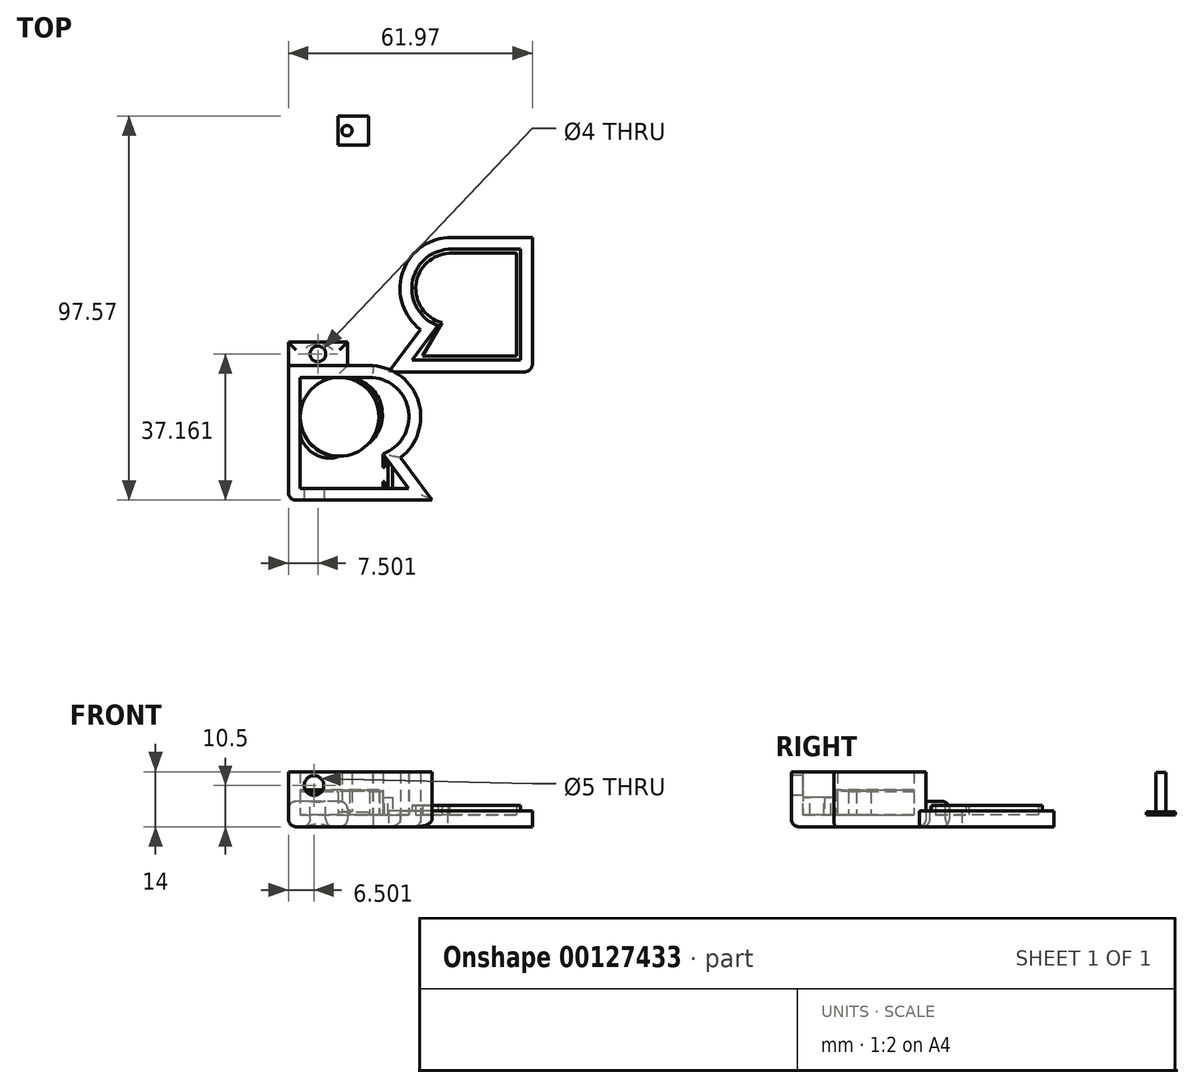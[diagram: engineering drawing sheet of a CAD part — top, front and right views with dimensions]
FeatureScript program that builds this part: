
annotation { "Feature Type Name" : "Feature", "Feature Type Description" : "" }
export const myFeature = defineFeature(function(context is Context, id is Id, definition is map)
    precondition{}
    {
        {
            var Q0;
            Q0=qCreatedBy(makeId("Top.planeOp"),FACE);
            var sketch = newSketch(context, id + "F0", { "sketchPlane" : qUnion([Q0])});
            skArc(sketch, "E0", {"start": v(-49.02, -36.56) * mm, "mid": v(-42.48, -25.81) * mm, "end": v(-51.63, -17.18) * mm});
            skLineSegment(sketch, "E1", {"start": v(-51.63, -17.18) * mm, "end": v(-70.02, -17.18) * mm});
            skLineSegment(sketch, "E2", {"start": v(-70.02, -17.18) * mm, "end": v(-70.02, -45.34) * mm});
            skLineSegment(sketch, "E3", {"start": v(-49.02, -36.56) * mm, "end": v(-42.48, -45.34) * mm});
            skPoint(sketch, "E3.endSnap0", {"position": v(-42.48, -25.81) * mm});
            skLineSegment(sketch, "E4", {"start": v(-70.02, -45.34) * mm, "end": v(-42.48, -45.34) * mm});
            skLineSegment(sketch, "E5", {"start": v(-62.53, -36.96) * mm, "end": v(-62.53, -43.4) * mm});
            skLineSegment(sketch, "E6", {"start": v(-62.53, -43.4) * mm, "end": v(-53.92, -43.4) * mm});
            skLineSegment(sketch, "E7", {"start": v(-53.92, -43.4) * mm, "end": v(-58.71, -36.96) * mm});
            skLineSegment(sketch, "E8", {"start": v(-58.71, -36.96) * mm, "end": v(-62.53, -36.96) * mm});
            skLineSegment(sketch, "E9", {"start": v(-62.53, -20.07) * mm, "end": v(-62.52, -34.24) * mm});
            skLineSegment(sketch, "E10", {"start": v(-62.52, -34.24) * mm, "end": v(-52.4, -34.23) * mm});
            skLineSegment(sketch, "E11", {"start": v(-52.4, -20.07) * mm, "end": v(-62.53, -20.07) * mm});
            skArc(sketch, "E12", {"start": v(-52.4, -34.23) * mm, "mid": v(-45.31, -27.15) * mm, "end": v(-52.4, -20.07) * mm});
            skSolve(sketch);
        }
        {
            var Q0;
            Q0 = qSketchRegion(id + "F0", true);
            var Q1;
            Q1=makeQuery(id+"F0.imprint","IMPRINT",FACE,{"disambiguationData":[TD([[makeQuery(id+"F0.imprint","IMPRINT",EDGE,{"derivedFrom":sQuery(id+"F0.wireOp",EDGE,"E9")}),1.0]])]});
            var Q2;
            Q2=makeQuery(id+"F0.imprint","IMPRINT",FACE,{"disambiguationData":[TD([[makeQuery(id+"F0.imprint","IMPRINT",EDGE,{"derivedFrom":sQuery(id+"F0.wireOp",EDGE,"E5")}),1.0]])]});
            extrude(context, id + "F1", {"entities" : qUnion([Q0, Q1, Q2]), "depth" : 11 * mm});
        }
        {
            var Q0;
            Q0=makeQuery(id+"F1.opExtrude","CAP_FACE",FACE,{"disambiguationData":[OSD([sQuery(id+"F0.wireOp",EDGE,"E0"),sQuery(id+"F0.wireOp",EDGE,"E1"),sQuery(id+"F0.wireOp",EDGE,"E2"),sQuery(id+"F0.wireOp",EDGE,"E3"),sQuery(id+"F0.wireOp",EDGE,"E4")])],"isStart":false});
            shell(context, id + "F2", {"entities" : qUnion([Q0]), "thickness" : 3 * mm, "oppositeDirection" : true});
        }
        {
            var Q0;
            Q0=makeQuery(id+"F1.opExtrude","SWEPT_FACE",FACE,{"disambiguationData":[OSD([sQuery(id+"F0.wireOp",EDGE,"E4")])]});
            var sketch = newSketch(context, id + "F3", { "sketchPlane" : qUnion([Q0])});
            skCircle(sketch, "E13", {"center": v(-66.52, 7.5) * mm, "radius": 2.5 * mm});
            skSolve(sketch);
        }
        {
            var Q0;
            Q0=makeQuery(id+"F3.imprint","IMPRINT",FACE,{"disambiguationData":[TD([[makeQuery(id+"F3.imprint","IMPRINT",EDGE,{"derivedFrom":sQuery(id+"F3.wireOp",EDGE,"E13")}),1.0]])]});
            extrude(context, id + "F4", {"entities" : qUnion([Q0]), "operationType" : NewBodyOperationType.REMOVE, "oppositeDirection" : true, "depth" : 3 * mm});
        }
        {
            var Q0;
            Q0=makeQuery(id+"F2.opShell","OFFSET_FACE",FACE,{"disambiguationData":[OSD([sQuery(id+"F0.wireOp",EDGE,"E0"),sQuery(id+"F0.wireOp",EDGE,"E1"),sQuery(id+"F0.wireOp",EDGE,"E2"),sQuery(id+"F0.wireOp",EDGE,"E3"),sQuery(id+"F0.wireOp",EDGE,"E4")])]});
            var sketch = newSketch(context, id + "F5", { "sketchPlane" : qUnion([Q0])});
            skCircle(sketch, "E14", {"center": v(-60.02, -27.18) * mm, "radius": 10 * mm});
            skSolve(sketch);
        }
        {
            var Q0;
            Q0=makeQuery(id+"F5.imprint","IMPRINT",FACE,{"disambiguationData":[TD([[makeQuery(id+"F5.imprint","IMPRINT",EDGE,{"derivedFrom":sQuery(id+"F5.wireOp",EDGE,"E14")}),1.0]])]});
            extrude(context, id + "F6", {"entities" : qUnion([Q0]), "depth" : 6.4 * mm});
        }
        {
            var Q0;
            Q0=makeQuery(id+"F2.opShell","OFFSET_FACE",FACE,{"disambiguationData":[OSD([sQuery(id+"F0.wireOp",EDGE,"E0"),sQuery(id+"F0.wireOp",EDGE,"E1"),sQuery(id+"F0.wireOp",EDGE,"E2"),sQuery(id+"F0.wireOp",EDGE,"E3"),sQuery(id+"F0.wireOp",EDGE,"E4")])]});
            var sketch = newSketch(context, id + "F7", { "sketchPlane" : qUnion([Q0])});
            skLineSegment(sketch, "E15", {"start": v(-49.02, -36.56) * mm, "end": v(-49.02, -45.34) * mm});
            skLineSegment(sketch, "E16", {"start": v(-49.02, -36.56) * mm, "end": v(-46.52, -39.92) * mm});
            skLineSegment(sketch, "E17", {"start": v(-46.52, -39.92) * mm, "end": v(-46.52, -45.34) * mm});
            skSolve(sketch);
        }
        {
            var Q0;
            {var subQ0=sQuery(id+"F7.wireOp",EDGE,"E15");Q0=makeQuery(id+"F7.imprint","IMPRINT",FACE,{"disambiguationData":[TD([[makeQuery(id+"F7.imprint","IMPRINT",EDGE,{"derivedFrom":subQ0}),1.0]])]});}
            var Q1;
            Q1=sQuery(id+"F7.wireOp",EDGE,"uWyAT9Lh-1afm-2KB9-5gJl-7Iz2kAB5TRkk");
            var Q2;
            Q2=makeQuery(id+"F1.opExtrude","CAP_FACE",FACE,{"disambiguationData":[OSD([sQuery(id+"F0.wireOp",EDGE,"E0"),sQuery(id+"F0.wireOp",EDGE,"E1"),sQuery(id+"F0.wireOp",EDGE,"E2"),sQuery(id+"F0.wireOp",EDGE,"E3"),sQuery(id+"F0.wireOp",EDGE,"E4")])],"isStart":false});
            extrude(context, id + "F8", {"entities" : qUnion([Q0]), "surfaceEntities" : qUnion([Q1]), "endBoundEntityFace" : qUnion([Q2]), "depth" : 4.5 * mm});
        }
        {
            var Q0;
            Q0=makeQuery(id+"F1.opExtrude","SWEPT_FACE",FACE,{"disambiguationData":[OSD([sQuery(id+"F0.wireOp",EDGE,"E1")])]});
            var sketch = newSketch(context, id + "F9", { "sketchPlane" : qUnion([Q0])});
            skLineSegment(sketch, "E18.bottom", {"start": v(58.02, 3.5) * mm, "end": v(73.02, 3.5) * mm});
            skLineSegment(sketch, "E18.top", {"start": v(58.02, -3) * mm, "end": v(73.02, -3) * mm});
            skLineSegment(sketch, "E18.left", {"start": v(58.02, 3.5) * mm, "end": v(58.02, -3) * mm});
            skLineSegment(sketch, "E18.right", {"start": v(73.02, 3.5) * mm, "end": v(73.02, -3) * mm});
            skSolve(sketch);
        }
        {
            var Q0;
            Q0=makeQuery(id+"F9.imprint","IMPRINT",FACE,{"disambiguationData":[TD([[makeQuery(id+"F9.imprint","IMPRINT",EDGE,{"derivedFrom":sQuery(id+"F9.wireOp",EDGE,"E18.bottom")}),-1.0]])]});
            extrude(context, id + "F10", {"entities" : qUnion([Q0]), "operationType" : NewBodyOperationType.ADD, "depth" : 6 * mm});
        }
        {
            var Q0;
            Q0=makeQuery(id+"F10.opExtrude","SWEPT_FACE",FACE,{"disambiguationData":[OSD([sQuery(id+"F9.wireOp",EDGE,"E18.bottom")])]});
            var sketch = newSketch(context, id + "F11", { "sketchPlane" : qUnion([Q0])});
            skCircle(sketch, "E19", {"center": v(-65.52, -11.18) * mm, "radius": 2 * mm});
            skPoint(sketch, "E20", {"position": v(-65.52, -8.18) * mm});
            skPoint(sketch, "E21", {"position": v(-73.02, -11.18) * mm});
            skSolve(sketch);
        }
        {
            var Q0;
            Q0=makeQuery(id+"F11.imprint","IMPRINT",FACE,{"disambiguationData":[TD([[makeQuery(id+"F11.imprint","IMPRINT",EDGE,{"derivedFrom":sQuery(id+"F11.wireOp",EDGE,"E19")}),1.0]])]});
            extrude(context, id + "F12", {"entities" : qUnion([Q0]), "operationType" : NewBodyOperationType.REMOVE, "endBound" : BoundingType.THROUGH_ALL, "oppositeDirection" : true, "depth" : 25 * mm});
        }
        {
            var Q0;
            Q0=makeQuery(id+"F12.boolean.opBoolean","COPY",EDGE,{"derivedFrom":makeQuery(id+"F12.opExtrude","CAP_EDGE",EDGE,{"disambiguationData":[OSD([sQuery(id+"F11.wireOp",EDGE,"E19")])],"isStart":true})});
            var Q1;
            Q1=makeQuery(id+"F12.boolean.opBoolean","INTERSECT",EDGE,{"derivedFrom":[makeQuery(id+"F10.boolean.opBoolean","MERGE",FACE,{"derivedFrom":[makeQuery(id+"F1.opExtrude","CAP_FACE",FACE,{"disambiguationData":[OSD([sQuery(id+"F0.wireOp",EDGE,"E0"),sQuery(id+"F0.wireOp",EDGE,"E1"),sQuery(id+"F0.wireOp",EDGE,"E2"),sQuery(id+"F0.wireOp",EDGE,"E3"),sQuery(id+"F0.wireOp",EDGE,"E4")])],"isStart":true}),makeQuery(id+"F10.opExtrude","SWEPT_FACE",FACE,{"disambiguationData":[OSD([sQuery(id+"F9.wireOp",EDGE,"E18.top")])]})]}),makeQuery(id+"F12.opExtrude","SWEPT_FACE",FACE,{"disambiguationData":[OSD([sQuery(id+"F11.wireOp",EDGE,"E19")])]})]});
            var Q2;
            Q2=makeQuery(id+"F10.opExtrude","SWEPT_EDGE",EDGE,{"disambiguationData":[OSD([sQuery(id+"F0.wireOp",EDGE,"E1"),sQuery(id+"F0.wireOp",EDGE,"E2"),sQuery(id+"F9.wireOp",EDGE,"E18.bottom"),sQuery(id+"F9.wireOp",EDGE,"E18.right")])]});
            var Q3;
            Q3=makeQuery(id+"F10.opExtrude","CAP_EDGE",EDGE,{"disambiguationData":[OSD([sQuery(id+"F9.wireOp",EDGE,"E18.bottom")])],"isStart":false});
            var Q4;
            Q4=makeQuery(id+"F10.opExtrude","SWEPT_EDGE",EDGE,{"disambiguationData":[OSD([sQuery(id+"F9.wireOp",EDGE,"E18.bottom"),sQuery(id+"F9.wireOp",EDGE,"E18.left")])]});
            var Q5;
            Q5=makeQuery(id+"F10.opExtrude","CAP_EDGE",EDGE,{"disambiguationData":[OSD([sQuery(id+"F9.wireOp",EDGE,"E18.top")])],"isStart":false});
            var Q6;
            Q6=makeQuery(id+"F10.opExtrude","SWEPT_EDGE",EDGE,{"disambiguationData":[OSD([sQuery(id+"F0.wireOp",EDGE,"E1"),sQuery(id+"F9.wireOp",EDGE,"E18.top"),sQuery(id+"F9.wireOp",EDGE,"E18.left")])]});
            var Q7;
            Q7=makeQuery(id+"F10.boolean.opBoolean","MERGE",FACE,{"derivedFrom":[makeQuery(id+"F1.opExtrude","CAP_FACE",FACE,{"disambiguationData":[OSD([sQuery(id+"F0.wireOp",EDGE,"E0"),sQuery(id+"F0.wireOp",EDGE,"E1"),sQuery(id+"F0.wireOp",EDGE,"E2"),sQuery(id+"F0.wireOp",EDGE,"E3"),sQuery(id+"F0.wireOp",EDGE,"E4")])],"isStart":true}),makeQuery(id+"F10.opExtrude","SWEPT_FACE",FACE,{"disambiguationData":[OSD([sQuery(id+"F9.wireOp",EDGE,"E18.top")])]})]});
            var Q8;
            Q8=makeQuery(id+"F1.opExtrude","SWEPT_EDGE",EDGE,{"disambiguationData":[OSD([sQuery(id+"F0.wireOp",EDGE,"E2"),sQuery(id+"F0.wireOp",EDGE,"E4")])]});
            fillet(context, id + "F13", {"entities" : qUnion([Q0, Q1, Q2, Q3, Q4, Q5, Q6, Q7, Q8]), "radius" : 2 * mm, "tangentPropagation" : true, "allowEdgeOverflow" : false});
        }
        {
            var Q0;
            Q0=makeQuery(id+"F8.opExtrude","CAP_FACE",FACE,{"disambiguationData":[OSD([sQuery(id+"F0.wireOp",EDGE,"E4"),sQuery(id+"F7.wireOp",EDGE,"E15"),sQuery(id+"F7.wireOp",EDGE,"9iCo8BHy-f28p-cC54-CTSm-TEKlpERLjaZK"),sQuery(id+"F7.wireOp",EDGE,"JoWHUIms-sXX3-WeBb-AUru-H7kbjBLy2FEL")])],"isStart":false});
            var sketch = newSketch(context, id + "F14", { "sketchPlane" : qUnion([Q0])});
            skLineSegment(sketch, "E22", {"start": v(-49.02, -40.09) * mm, "end": v(-48.55, -40.09) * mm});
            skLineSegment(sketch, "E23", {"start": v(-48.55, -40.09) * mm, "end": v(-48.55, -38.34) * mm});
            skLineSegment(sketch, "E24", {"start": v(-48.55, -38.34) * mm, "end": v(-47.75, -38.34) * mm});
            skLineSegment(sketch, "E25", {"start": v(-47.75, -38.34) * mm, "end": v(-47.75, -45.34) * mm});
            skLineSegment(sketch, "E26", {"start": v(-47.75, -45.34) * mm, "end": v(-48.55, -45.34) * mm});
            skLineSegment(sketch, "E27", {"start": v(-48.55, -45.34) * mm, "end": v(-48.55, -43.59) * mm});
            skLineSegment(sketch, "E28", {"start": v(-48.55, -43.59) * mm, "end": v(-49.02, -43.59) * mm});
            skLineSegment(sketch, "E29", {"start": v(-49.02, -43.59) * mm, "end": v(-49.02, -40.09) * mm});
            skSolve(sketch);
        }
        {
            var Q0;
            Q0=makeQuery(id+"F14.imprint","IMPRINT",FACE,{"disambiguationData":[TD([[makeQuery(id+"F14.imprint","IMPRINT",EDGE,{"derivedFrom":sQuery(id+"F14.wireOp",EDGE,"E22")}),-1.0]])]});
            var Q1;
            Q1=makeQuery(id+"F2.opShell","OFFSET_FACE",FACE,{"disambiguationData":[OSD([sQuery(id+"F0.wireOp",EDGE,"E0"),sQuery(id+"F0.wireOp",EDGE,"E1"),sQuery(id+"F0.wireOp",EDGE,"E2"),sQuery(id+"F0.wireOp",EDGE,"E3"),sQuery(id+"F0.wireOp",EDGE,"E4")])]});
            extrude(context, id + "F15", {"entities" : qUnion([Q0]), "operationType" : NewBodyOperationType.REMOVE, "endBound" : BoundingType.UP_TO_SURFACE, "oppositeDirection" : true, "endBoundEntityFace" : qUnion([Q1]), "depth" : 25 * mm});
        }
        {
            var Q0;
            Q0=makeQuery(id+"F2.opShell","OFFSET_FACE",FACE,{"disambiguationData":[OSD([sQuery(id+"F0.wireOp",EDGE,"E0"),sQuery(id+"F0.wireOp",EDGE,"E1"),sQuery(id+"F0.wireOp",EDGE,"E2"),sQuery(id+"F0.wireOp",EDGE,"E3"),sQuery(id+"F0.wireOp",EDGE,"E4")])]});
            var sketch = newSketch(context, id + "F16", { "sketchPlane" : qUnion([Q0])});
            skArc(sketch, "E30", {"start": v(-52.4, -33.8) * mm, "mid": v(-50.78, -23.1) * mm, "end": v(-59.84, -17.18) * mm});
            skArc(sketch, "E31", {"start": v(-52.4, -33.8) * mm, "mid": v(-49.97, -22.74) * mm, "end": v(-59.84, -17.18) * mm});
            skArc(sketch, "E32", {"start": v(-70.02, -28.1) * mm, "mid": v(-66.97, -34.57) * mm, "end": v(-60.37, -37.34) * mm});
            skArc(sketch, "E33", {"start": v(-70.02, -28.1) * mm, "mid": v(-67.86, -35.5) * mm, "end": v(-60.37, -37.34) * mm});
            skSolve(sketch);
        }
        {
            var Q0;
            {var subQ0=sQuery(id+"F16.wireOp",EDGE,"E30");Q0=makeQuery(id+"F16.imprint","IMPRINT",FACE,{"disambiguationData":[TD([[makeQuery(id+"F16.imprint","IMPRINT",EDGE,{"derivedFrom":subQ0}),-1.0]])]});}
            var Q1;
            {var subQ0=sQuery(id+"F16.wireOp",EDGE,"E32");Q1=makeQuery(id+"F16.imprint","IMPRINT",FACE,{"disambiguationData":[TD([[makeQuery(id+"F16.imprint","IMPRINT",EDGE,{"derivedFrom":subQ0}),-1.0]])]});}
            extrude(context, id + "F17", {"entities" : qUnion([Q0, Q1]), "operationType" : NewBodyOperationType.ADD, "depth" : 6 * mm});
        }
        {
            var Q0;
            Q0=qCreatedBy(makeId("Top.planeOp"),FACE);
            var sketch = newSketch(context, id + "F18", { "sketchPlane" : qUnion([Q0])});
            skLineSegment(sketch, "E34", {"start": v(-14.05, 15.4) * mm, "end": v(-14.05, -12.76) * mm});
            skLineSegment(sketch, "E35.MirrorCS", {"start": v(-32.43, 15.4) * mm, "end": v(-14.05, 15.4) * mm});
            skArc(sketch, "E36.MirrorCS", {"start": v(-35.05, -3.99) * mm, "mid": v(-41.58, 6.76) * mm, "end": v(-32.43, 15.4) * mm});
            skLineSegment(sketch, "E37.MirrorCS", {"start": v(-35.05, -3.99) * mm, "end": v(-41.58, -12.76) * mm});
            skLineSegment(sketch, "E38.MirrorCS", {"start": v(-14.05, -12.76) * mm, "end": v(-41.58, -12.76) * mm});
            skSolve(sketch);
        }
        {
            var Q0;
            Q0=makeQuery(id+"F18.imprint","IMPRINT",FACE,{"disambiguationData":[TD([[makeQuery(id+"F18.imprint","IMPRINT",EDGE,{"derivedFrom":sQuery(id+"F18.wireOp",EDGE,"E34")}),-1.0]])]});
            extrude(context, id + "F19", {"entities" : qUnion([Q0]), "depth" : 1 * mm});
        }
        {
            var Q0;
            Q0=makeQuery(id+"F19.opExtrude","CAP_FACE",FACE,{"disambiguationData":[OSD([sQuery(id+"F18.wireOp",EDGE,"E34"),sQuery(id+"F18.wireOp",EDGE,"E35.MirrorCS"),sQuery(id+"F18.wireOp",EDGE,"E36.MirrorCS"),sQuery(id+"F18.wireOp",EDGE,"E37.MirrorCS"),sQuery(id+"F18.wireOp",EDGE,"E38.MirrorCS")])],"isStart":false});
            shell(context, id + "F20", {"entities" : qUnion([Q0]), "thickness" : 3 * mm, "oppositeDirection" : true});
        }
        {
            var Q0;
            Q0=makeQuery(id+"F20.opShell","OFFSET_FACE",FACE,{"disambiguationData":[OSD([sQuery(id+"F18.wireOp",EDGE,"E34"),sQuery(id+"F18.wireOp",EDGE,"E35.MirrorCS"),sQuery(id+"F18.wireOp",EDGE,"E36.MirrorCS"),sQuery(id+"F18.wireOp",EDGE,"E37.MirrorCS"),sQuery(id+"F18.wireOp",EDGE,"E38.MirrorCS")])]});
            var sketch = newSketch(context, id + "F21", { "sketchPlane" : qUnion([Q0])});
            skLineSegment(sketch, "E39", {"start": v(-38.97, -11.76) * mm, "end": v(-34.05, -3.25) * mm});
            skArc(sketch, "E40", {"start": v(-32.04, 14.4) * mm, "mid": v(-40.62, 6.44) * mm, "end": v(-34.05, -3.25) * mm});
            skLineSegment(sketch, "E41", {"start": v(-32.04, 14.4) * mm, "end": v(-15.05, 14.4) * mm});
            skLineSegment(sketch, "E42", {"start": v(-15.05, 14.4) * mm, "end": v(-15.05, -11.76) * mm});
            skLineSegment(sketch, "E43", {"start": v(-15.05, -11.76) * mm, "end": v(-38.97, -11.76) * mm});
            skSolve(sketch);
        }
        {
            var Q0;
            Q0=makeQuery(id+"F21.imprint","IMPRINT",FACE,{"disambiguationData":[TD([[makeQuery(id+"F21.imprint","IMPRINT",EDGE,{"derivedFrom":sQuery(id+"F21.wireOp",EDGE,"E39")}),1.0]])]});
            extrude(context, id + "F22", {"entities" : qUnion([Q0]), "operationType" : NewBodyOperationType.ADD, "depth" : 2.5 * mm});
        }
        {
            var Q0;
            Q0=makeQuery(id+"F19.opExtrude","SWEPT_EDGE",EDGE,{"disambiguationData":[OSD([sQuery(id+"F18.wireOp",EDGE,"E34"),sQuery(id+"F18.wireOp",EDGE,"E38.MirrorCS")])]});
            fillet(context, id + "F23", {"entities" : qUnion([Q0]), "radius" : 2 * mm, "tangentPropagation" : true, "allowEdgeOverflow" : false});
        }
        {
            var Q0;
            Q0=qCreatedBy(makeId("Top.planeOp"),FACE);
            var sketch = newSketch(context, id + "F24", { "sketchPlane" : qUnion([Q0])});
            skLineSegment(sketch, "E44.bottom", {"start": v(-60.4, 49.23) * mm, "end": v(-52.7, 49.23) * mm});
            skLineSegment(sketch, "E44.top", {"start": v(-60.4, 41.83) * mm, "end": v(-52.7, 41.83) * mm});
            skLineSegment(sketch, "E44.left", {"start": v(-60.4, 49.23) * mm, "end": v(-60.4, 41.83) * mm});
            skLineSegment(sketch, "E44.right", {"start": v(-52.7, 49.23) * mm, "end": v(-52.7, 41.83) * mm});
            skPoint(sketch, "E45.centerSnap0", {"position": v(-52.7, 45.53) * mm});
            skSolve(sketch);
        }
        {
            var Q0;
            Q0=makeQuery(id+"F24.imprint","IMPRINT",FACE,{"disambiguationData":[TD([[makeQuery(id+"F24.imprint","IMPRINT",EDGE,{"derivedFrom":sQuery(id+"F24.wireOp",EDGE,"E44.bottom")}),-1.0]])]});
            extrude(context, id + "F25", {"entities" : qUnion([Q0]), "depth" : 0.8 * mm});
        }
        {
            var Q0;
            Q0=makeQuery(id+"F25.opExtrude","CAP_FACE",FACE,{"disambiguationData":[OSD([sQuery(id+"F24.wireOp",EDGE,"E44.bottom"),sQuery(id+"F24.wireOp",EDGE,"E44.top"),sQuery(id+"F24.wireOp",EDGE,"E44.left"),sQuery(id+"F24.wireOp",EDGE,"E44.right")])],"isStart":false});
            var sketch = newSketch(context, id + "F26", { "sketchPlane" : qUnion([Q0])});
            skCircle(sketch, "E46", {"center": v(-58.13, 45.53) * mm, "radius": 1.3 * mm});
            skPoint(sketch, "E47", {"position": v(-60.4, 45.53) * mm});
            skSolve(sketch);
        }
        {
            var Q0;
            Q0=makeQuery(id+"F26.imprint","IMPRINT",FACE,{"disambiguationData":[TD([[makeQuery(id+"F26.imprint","IMPRINT",EDGE,{"derivedFrom":sQuery(id+"F26.wireOp",EDGE,"E46")}),1.0]])]});
            extrude(context, id + "F27", {"entities" : qUnion([Q0]), "operationType" : NewBodyOperationType.ADD, "depth" : 10 * mm});
        }
    });
